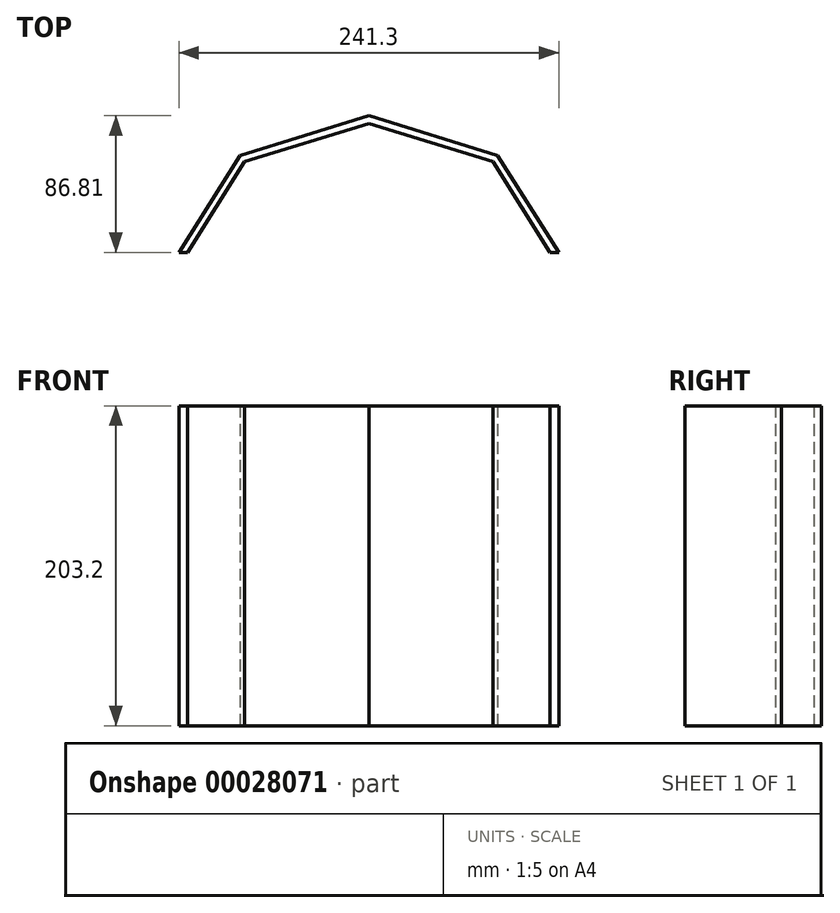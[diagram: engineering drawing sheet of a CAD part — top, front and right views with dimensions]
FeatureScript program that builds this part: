
annotation { "Feature Type Name" : "Feature", "Feature Type Description" : "" }
export const myFeature = defineFeature(function(context is Context, id is Id, definition is map)
    precondition{}
    {
        {
            var Q0;
            Q0=qCreatedBy(makeId("Top.planeOp"),FACE);
            var sketch = newSketch(context, id + "F0", { "sketchPlane" : qUnion([Q0])});
            skLineSegment(sketch, "E0", {"start": v(-120.65, 0) * mm, "end": v(-81.8, 61.5) * mm});
            skLineSegment(sketch, "E1", {"start": v(-81.8, 61.5) * mm, "end": v(0, 86.8) * mm});
            skLineSegment(sketch, "E2.MirrorCS", {"start": v(81.8, 61.5) * mm, "end": v(0, 86.8) * mm});
            skLineSegment(sketch, "E3.MirrorCS", {"start": v(120.65, 0) * mm, "end": v(81.8, 61.5) * mm});
            skLineSegment(sketch, "E4.0", {"start": v(-115.14, 0) * mm, "end": v(-78.79, 57.56) * mm});
            skLineSegment(sketch, "E4.1", {"start": v(-78.79, 57.56) * mm, "end": v(0, 81.93) * mm});
            skLineSegment(sketch, "E4.2", {"start": v(78.79, 57.56) * mm, "end": v(0, 81.93) * mm});
            skLineSegment(sketch, "E4.3", {"start": v(115.14, 0) * mm, "end": v(78.79, 57.56) * mm});
            skLineSegment(sketch, "E5", {"start": v(-120.65, 0) * mm, "end": v(-115.14, 0) * mm});
            skLineSegment(sketch, "E6", {"start": v(-115.14, 0) * mm, "end": v(115.14, 0) * mm, "construction": true});
            skLineSegment(sketch, "E7", {"start": v(115.14, 0) * mm, "end": v(120.65, 0) * mm});
            skSolve(sketch);
        }
        {
            var Q0;
            Q0=makeQuery(id+"F0.imprint","IMPRINT",FACE,{"disambiguationData":[TD([[makeQuery(id+"F0.imprint","IMPRINT",EDGE,{"derivedFrom":sQuery(id+"F0.wireOp",EDGE,"E0")}),-1.0]])]});
            extrude(context, id + "F1", {"entities" : qUnion([Q0]), "depth" : 203.2 * mm});
        }
    });
